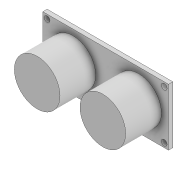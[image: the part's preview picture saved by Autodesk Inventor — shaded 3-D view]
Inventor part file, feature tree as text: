
AUTODESK INVENTOR PART (.ipt)
format: ipt  version: 2022 (Build 260153000, 153)  size: 123,904 bytes
history: native  units: mm
features: sketch x3, extrude x2, hole x1
ambient origin geometry x8: Origin, YZ Plane, XZ Plane, XY Plane, X Axis, Y Axis, Z Axis, Center Point
bodies: Solid1 (feature_tree)
feature tree (6):
  extrude  "Extrusion1"  Depth=20.0mm
  extrude  "Extrusion2"  Depth=1.5mm
  hole  "Hole1"  [1 undecoded]
  sketch  "Sketch1"  dims[d0=44.0mm d1=20.0mm]
  sketch  "Sketch2"  dims[d2=1.5mm d3=0.0mm d4=16.0mm]
  sketch  "Sketch3"  dims[d5=2.5mm d6=12.5mm d7=0.0mm d8=0.5mm d9=0.5mm d10=0.5mm d11=0.5mm d12=2.0mm d13=2.0mm d14=2.0mm d15=2.0mm d16=2.0mm d17=6.0mm d18=4.0mm d19=2.0mm d20=90.0deg d21=6.0mm d22=0.0mm]
note: 1 required parameter value undecoded (feature->parameter linkage not recoverable at this tier; creation-order binding heuristic only, values carry confidence <= 0.55)
